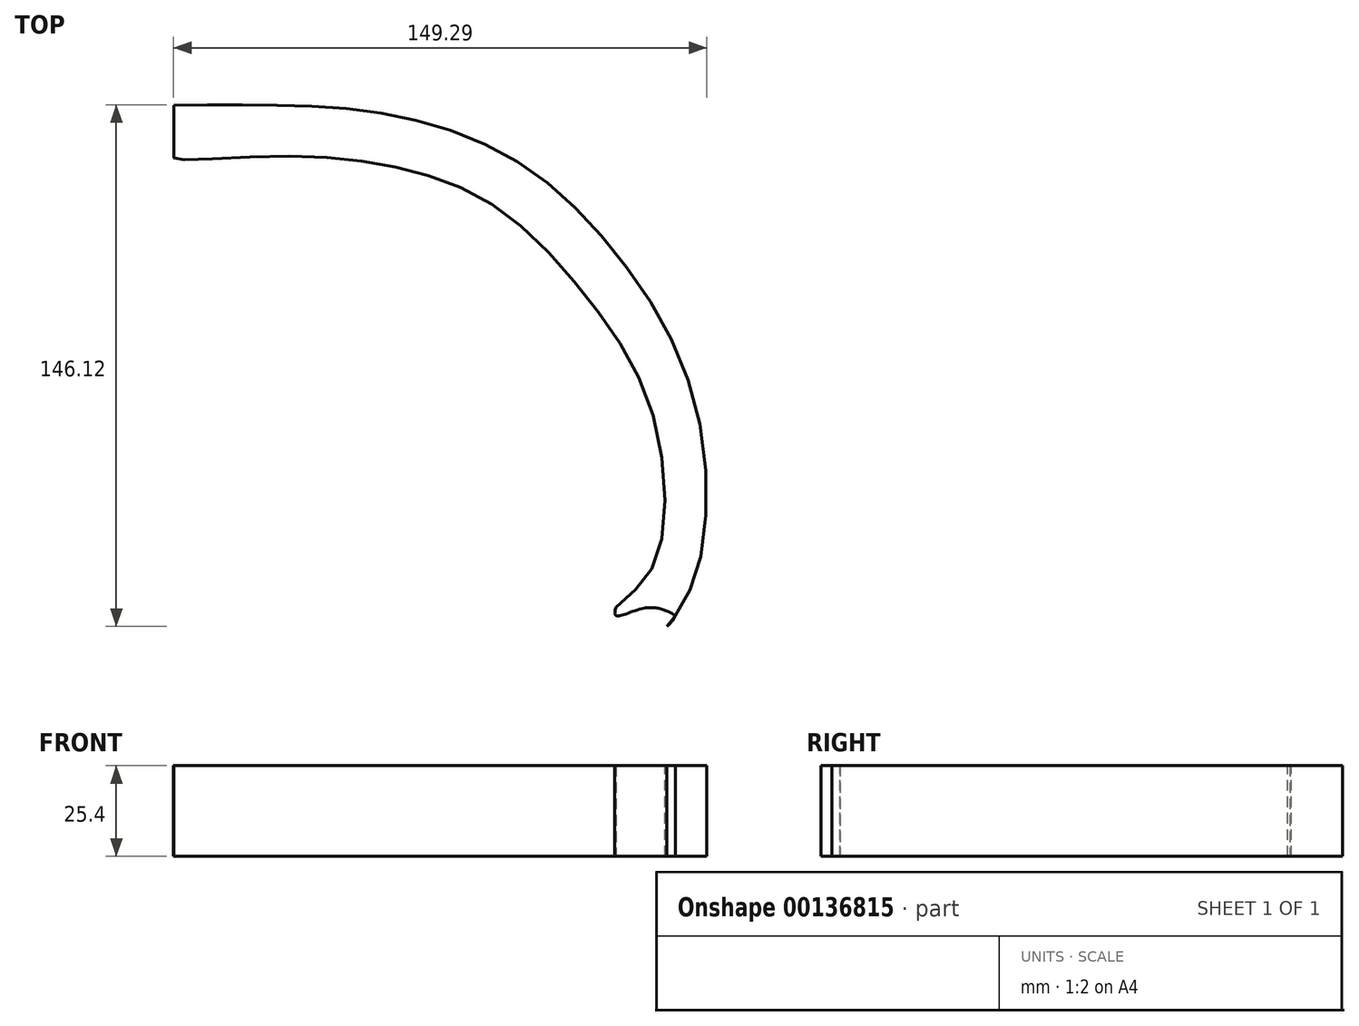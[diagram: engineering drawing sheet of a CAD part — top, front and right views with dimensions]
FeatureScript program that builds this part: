
annotation { "Feature Type Name" : "Feature", "Feature Type Description" : "" }
export const myFeature = defineFeature(function(context is Context, id is Id, definition is map)
    precondition{}
    {
        {
            var Q0;
            Q0=qCreatedBy(makeId("Top.planeOp"),FACE);
            var sketch = newSketch(context, id + "F0", { "sketchPlane" : qUnion([Q0])});
            skFitSpline(sketch, "E0", {"points": [v(0, 32.36) * mm, v(11.42, 46.22) * mm, v(10.43, 86.04) * mm, v(-8.25, 119.47) * mm, v(-34.3, 145.03) * mm, v(-62.32, 155.84) * mm, v(-94.28, 158.8) * mm, v(-122.3, 157.81) * mm, v(-123.83, 158.3) * mm], "startDerivative": vector(132.33, 115.6) * mm, "endDerivative": vector(13.54, 29.9) * mm});
            skLineSegment(sketch, "E1", {"start": v(-123.83, 158.3) * mm, "end": v(-123.83, 172.98) * mm});
            skPoint(sketch, "E2.1.internal.orphan", {"position": v(-92.31, 172.98) * mm});
            skFitSpline(sketch, "E3", {"points": [v(-123.83, 172.98) * mm, v(-92.31, 172.98) * mm, v(-60.6, 169.87) * mm, v(-27.6, 157.22) * mm, v(0, 131.52) * mm, v(22.54, 88.49) * mm, v(21.95, 40.19) * mm, v(10.54, 22.95) * mm], "startDerivative": vector(226.58, 4.9) * mm, "endDerivative": vector(-114.74, -120.4) * mm});
            skPoint(sketch, "E4.end.orphan", {"position": v(5.38, 35.09) * mm});
            skPoint(sketch, "E5.start.orphan", {"position": v(0, 38.76) * mm});
            skFitSpline(sketch, "E6.trimOffspring", {"points": [v(-21.75, 1.93) * mm, v(-10.52, 13.26) * mm, v(16.72, 30.58) * mm, v(10.41, 34.12) * mm, v(5.34, 27.93) * mm, v(-8.28, 19.35) * mm, v(-21.92, 13.64) * mm, v(-28.45, 1.65) * mm], "startDerivative": vector(44.21, 81.23) * mm, "endDerivative": vector(-41.6, -109.42) * mm});
            skLineSegment(sketch, "E7.trimOffspring", {"start": v(7.91, 32.16) * mm, "end": v(7.91, 32.16) * mm});
            skPoint(sketch, "E8.end.orphan", {"position": v(4.62, 26.18) * mm});
            skFitSpline(sketch, "E9", {"points": [v(16.66, 30.1) * mm, v(7.91, 32.16) * mm, v(0, 30.1) * mm, v(0, 32.36) * mm], "startDerivative": vector(-19.9, 12.26) * mm, "endDerivative": vector(3.1, 11.9) * mm});
            skSolve(sketch);
        }
        {
            var Q0;
            Q0 = qSketchRegion(id + "F0", true);
            extrude(context, id + "F1", {"entities" : qUnion([Q0]), "depth" : 25.4 * mm});
        }
    });
